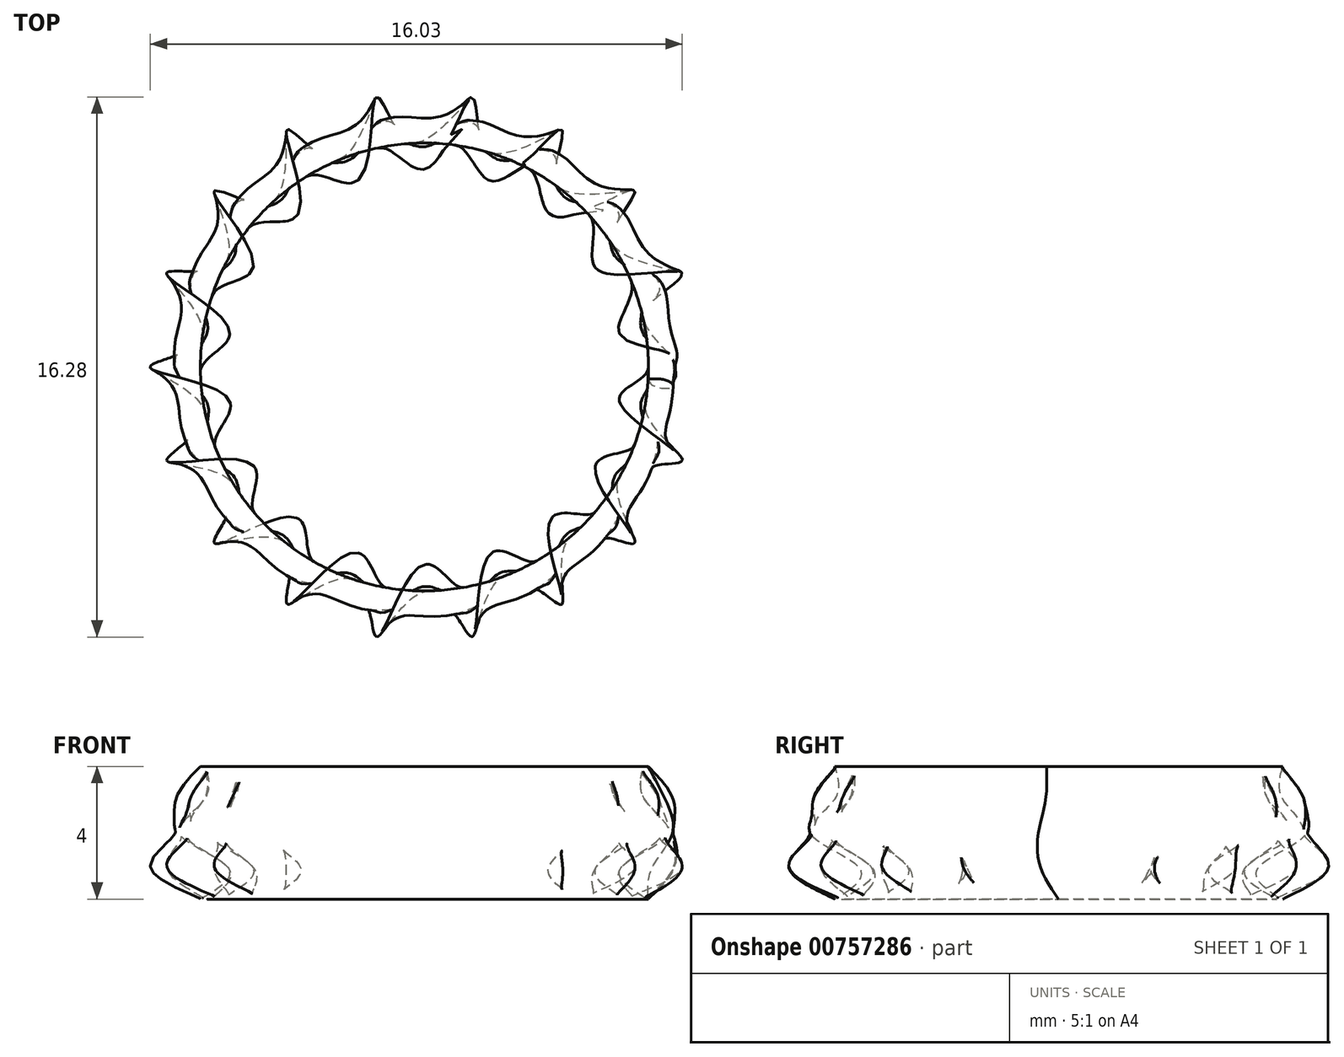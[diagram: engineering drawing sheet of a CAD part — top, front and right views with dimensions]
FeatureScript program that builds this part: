
annotation { "Feature Type Name" : "Feature", "Feature Type Description" : "" }
export const myFeature = defineFeature(function(context is Context, id is Id, definition is map)
    precondition{}
    {
        {
            var Q0;
            Q0=qCreatedBy(makeId("Top.planeOp"),FACE);
            var sketch = newSketch(context, id + "F0", { "sketchPlane" : qUnion([Q0])});
            skCircle(sketch, "E0", {"center": v(0, 0) * mm, "radius": 7.5 * mm});
            skCircle(sketch, "E1", {"center": v(0, 0) * mm, "radius": 6.75 * mm});
            skSolve(sketch);
        }
        {
            var Q0;
            Q0=qCreatedBy(makeId("Top.planeOp"),FACE);
            cPlane(context, id + "F1", {"entities" : qUnion([Q0]), "cplaneType" : CPlaneType.OFFSET, "offset" : 1 * mm, "width" : 150 * mm, "height" : 150 * mm});
        }
        {
            var Q0;
            Q0=qCreatedBy(id+"F1.planeOp",FACE);
            var sketch = newSketch(context, id + "F2", { "sketchPlane" : qUnion([Q0])});
            skCircle(sketch, "E2.0", {"center": v(0, 0) * mm, "radius": 6.75 * mm});
            skCircle(sketch, "E3.0", {"center": v(0, 0) * mm, "radius": 7.5 * mm});
            skPoint(sketch, "E4", {"position": v(7.5, 0) * mm});
            skPoint(sketch, "E5", {"position": v(6.75, 0) * mm});
            skLineSegment(sketch, "E6", {"start": v(7.5, 0) * mm, "end": v(6.75, 0) * mm});
            skLineSegment(sketch, "E7.1.0", {"start": v(7.39, -1.3) * mm, "end": v(6.65, -1.17) * mm});
            skLineSegment(sketch, "E7.2.0", {"start": v(7.05, -2.57) * mm, "end": v(6.34, -2.3) * mm});
            skLineSegment(sketch, "E7.3.0", {"start": v(6.5, -3.75) * mm, "end": v(5.85, -3.37) * mm});
            skLineSegment(sketch, "E7.4.0", {"start": v(5.75, -4.82) * mm, "end": v(5.17, -4.34) * mm});
            skLineSegment(sketch, "E7.5.0", {"start": v(4.82, -5.75) * mm, "end": v(4.34, -5.17) * mm});
            skLineSegment(sketch, "E7.6.0", {"start": v(3.75, -6.5) * mm, "end": v(3.37, -5.85) * mm});
            skLineSegment(sketch, "E7.7.0", {"start": v(2.57, -7.05) * mm, "end": v(2.3, -6.34) * mm});
            skLineSegment(sketch, "E7.8.0", {"start": v(1.3, -7.39) * mm, "end": v(1.17, -6.65) * mm});
            skLineSegment(sketch, "E7.9.0", {"start": v(0, -7.5) * mm, "end": v(0, -6.75) * mm});
            skLineSegment(sketch, "E7.10.0", {"start": v(-1.3, -7.39) * mm, "end": v(-1.17, -6.65) * mm});
            skLineSegment(sketch, "E7.11.0", {"start": v(-2.57, -7.05) * mm, "end": v(-2.3, -6.34) * mm});
            skLineSegment(sketch, "E7.12.0", {"start": v(-3.75, -6.5) * mm, "end": v(-3.38, -5.85) * mm});
            skLineSegment(sketch, "E7.13.0", {"start": v(-4.82, -5.75) * mm, "end": v(-4.34, -5.17) * mm});
            skLineSegment(sketch, "E7.14.0", {"start": v(-5.75, -4.82) * mm, "end": v(-5.17, -4.34) * mm});
            skLineSegment(sketch, "E7.15.0", {"start": v(-6.5, -3.75) * mm, "end": v(-5.85, -3.38) * mm});
            skLineSegment(sketch, "E7.16.0", {"start": v(-7.05, -2.57) * mm, "end": v(-6.34, -2.3) * mm});
            skLineSegment(sketch, "E7.17.0", {"start": v(-7.39, -1.3) * mm, "end": v(-6.65, -1.17) * mm});
            skLineSegment(sketch, "E7.18.0", {"start": v(-7.5, 0) * mm, "end": v(-6.75, 0) * mm});
            skLineSegment(sketch, "E7.19.0", {"start": v(-7.39, 1.3) * mm, "end": v(-6.65, 1.17) * mm});
            skLineSegment(sketch, "E7.20.0", {"start": v(-7.05, 2.57) * mm, "end": v(-6.34, 2.3) * mm});
            skLineSegment(sketch, "E7.21.0", {"start": v(-6.5, 3.75) * mm, "end": v(-5.85, 3.37) * mm});
            skLineSegment(sketch, "E7.22.0", {"start": v(-5.75, 4.82) * mm, "end": v(-5.17, 4.34) * mm});
            skLineSegment(sketch, "E7.23.0", {"start": v(-4.82, 5.75) * mm, "end": v(-4.34, 5.17) * mm});
            skLineSegment(sketch, "E7.24.0", {"start": v(-3.75, 6.5) * mm, "end": v(-3.37, 5.85) * mm});
            skLineSegment(sketch, "E7.25.0", {"start": v(-2.57, 7.05) * mm, "end": v(-2.3, 6.34) * mm});
            skLineSegment(sketch, "E7.26.0", {"start": v(-1.3, 7.39) * mm, "end": v(-1.17, 6.65) * mm});
            skLineSegment(sketch, "E7.27.0", {"start": v(0, 7.5) * mm, "end": v(0, 6.75) * mm});
            skLineSegment(sketch, "E7.28.0", {"start": v(1.3, 7.39) * mm, "end": v(1.17, 6.65) * mm});
            skLineSegment(sketch, "E7.29.0", {"start": v(2.57, 7.05) * mm, "end": v(2.3, 6.34) * mm});
            skLineSegment(sketch, "E7.30.0", {"start": v(3.75, 6.5) * mm, "end": v(3.37, 5.85) * mm});
            skLineSegment(sketch, "E7.31.0", {"start": v(4.82, 5.75) * mm, "end": v(4.34, 5.17) * mm});
            skLineSegment(sketch, "E7.32.0", {"start": v(5.75, 4.82) * mm, "end": v(5.17, 4.34) * mm});
            skLineSegment(sketch, "E7.33.0", {"start": v(6.5, 3.75) * mm, "end": v(5.85, 3.37) * mm});
            skLineSegment(sketch, "E7.34.0", {"start": v(7.05, 2.57) * mm, "end": v(6.34, 2.3) * mm});
            skLineSegment(sketch, "E7.35.0", {"start": v(7.39, 1.3) * mm, "end": v(6.65, 1.17) * mm});
            skLineSegment(sketch, "E7.anchor1", {"start": v(0, 0) * mm, "end": v(6.75, 0) * mm, "construction": true});
            skLineSegment(sketch, "E7.anchor2", {"start": v(0, 0) * mm, "end": v(6.75, 0) * mm, "construction": true});
            skFitSpline(sketch, "E8", {"points": [v(7.5, 0) * mm, v(6.65, -1.17) * mm, v(7.05, -2.57) * mm, v(5.85, -3.37) * mm, v(5.75, -4.82) * mm, v(4.34, -5.17) * mm, v(3.75, -6.5) * mm, v(2.3, -6.34) * mm, v(1.3, -7.39) * mm, v(0, -6.75) * mm, v(-1.3, -7.39) * mm, v(-2.3, -6.34) * mm, v(-3.75, -6.5) * mm, v(-4.34, -5.17) * mm, v(-5.75, -4.82) * mm, v(-5.85, -3.37) * mm, v(-7.05, -2.57) * mm, v(-6.65, -1.17) * mm, v(-7.5, 0) * mm, v(-6.65, 1.17) * mm, v(-7.05, 2.57) * mm, v(-5.85, 3.37) * mm, v(-5.75, 4.82) * mm, v(-4.34, 5.17) * mm, v(-3.75, 6.5) * mm, v(-2.3, 6.34) * mm, v(-1.3, 7.39) * mm, v(0, 6.75) * mm, v(1.3, 7.39) * mm, v(2.3, 6.34) * mm, v(3.75, 6.5) * mm, v(4.34, 5.17) * mm, v(5.75, 4.82) * mm, v(5.85, 3.38) * mm, v(7.05, 2.57) * mm, v(6.65, 1.17) * mm, v(7.5, 0) * mm]});
            skSolve(sketch);
        }
        {
            var Q0;
            Q0=qCreatedBy(makeId("Top.planeOp"),FACE);
            cPlane(context, id + "F3", {"entities" : qUnion([Q0]), "cplaneType" : CPlaneType.OFFSET, "offset" : 1 * mm, "oppositeDirection" : true, "width" : 150 * mm, "height" : 150 * mm});
        }
        {
            var Q0;
            Q0=qCreatedBy(id+"F3.planeOp",FACE);
            var sketch = newSketch(context, id + "F4", { "sketchPlane" : qUnion([Q0])});
            skFitSpline(sketch, "E9.0", {"points": [v(7.5, 0) * mm, v(7.5, -0.35) * mm, v(5.96, -1.05) * mm, v(7.77, -2.83) * mm, v(5.24, -3.03) * mm, v(6.33, -5.32) * mm, v(3.9, -4.64) * mm, v(4.13, -7.16) * mm, v(2.07, -5.69) * mm, v(1.44, -8.14) * mm, v(0, -6.05) * mm, v(-1.44, -8.14) * mm, v(-2.07, -5.69) * mm, v(-4.13, -7.16) * mm, v(-3.9, -4.64) * mm, v(-6.33, -5.32) * mm, v(-5.24, -3.03) * mm, v(-7.77, -2.83) * mm, v(-5.96, -1.05) * mm, v(-8.27, 0) * mm, v(-5.96, 1.05) * mm, v(-7.77, 2.83) * mm, v(-5.24, 3.03) * mm, v(-6.33, 5.32) * mm, v(-3.9, 4.64) * mm, v(-4.13, 7.16) * mm, v(-2.07, 5.69) * mm, v(-1.44, 8.14) * mm, v(0, 6.05) * mm, v(1.44, 8.14) * mm, v(2.07, 5.69) * mm, v(4.13, 7.16) * mm, v(3.9, 4.64) * mm, v(6.33, 5.32) * mm, v(5.24, 3.03) * mm, v(7.77, 2.83) * mm, v(5.96, 1.05) * mm, v(7.5, 0.35) * mm, v(7.5, 0) * mm]});
            skSolve(sketch);
        }
        {
            var Q0;
            Q0=qCreatedBy(id+"F3.planeOp",FACE);
            cPlane(context, id + "F5", {"entities" : qUnion([Q0]), "cplaneType" : CPlaneType.OFFSET, "offset" : 1 * mm, "oppositeDirection" : true, "width" : 150 * mm, "height" : 150 * mm});
        }
        {
            var Q0;
            Q0=qCreatedBy(id+"F5.planeOp",FACE);
            var sketch = newSketch(context, id + "F6", { "sketchPlane" : qUnion([Q0])});
            skCircle(sketch, "E10.0", {"center": v(0, 0) * mm, "radius": 6.75 * mm});
            skSolve(sketch);
        }
        {
            var Q0;
            Q0=qCreatedBy(id+"F1.planeOp",FACE);
            cPlane(context, id + "F7", {"entities" : qUnion([Q0]), "cplaneType" : CPlaneType.OFFSET, "offset" : 1 * mm, "width" : 150 * mm, "height" : 150 * mm});
        }
        {
            var Q0;
            Q0=qCreatedBy(id+"F7.planeOp",FACE);
            var sketch = newSketch(context, id + "F8", { "sketchPlane" : qUnion([Q0])});
            skCircle(sketch, "E11.0", {"center": v(0, 0) * mm, "radius": 6.75 * mm});
            skSolve(sketch);
        }
        {
            var Q0;
            Q0=sQuery(id+"F6.wireOp",EDGE,"E10.0");
            var Q1;
            Q1=sQuery(id+"F4.wireOp",EDGE,"E9.0");
            var Q2;
            Q2=sQuery(id+"F0.wireOp",EDGE,"E0");
            var Q3;
            Q3=sQuery(id+"F2.wireOp",EDGE,"E8");
            var Q4;
            Q4=sQuery(id+"F8.wireOp",EDGE,"E11.0");
            loft(context, id + "F9", {"bodyType" : ToolBodyType.SURFACE, "wireProfilesArray" : [{ "wireProfileEntities" : qUnion([Q0]) }, { "wireProfileEntities" : qUnion([Q1]) }, { "wireProfileEntities" : qUnion([Q2]) }, { "wireProfileEntities" : qUnion([Q3]) }, { "wireProfileEntities" : qUnion([Q4]) }]});
        }
    });
